# Revit family: Prises non verrouillées saillies 200_250V
name_source: partatom
category: Installations électriques
revit_build: Autodesk Revit 2018 (Build: 20170223_1515(x64)
units: mm (PartAtom-declared; Revit-internal decimal feet)

## family parameters
Conserver l'orientation des annotations = Non
Cote de connecteur circulaire = Utiliser le diamètre
Couper avec des vides une fois chargée = Non
Hôte = Face
Partagée = Non
Point de calcul de pièce = Non
Type d'élément = Normal

## types (17) — shared parameters
Couleur caractéristique = bleu
Elévation par défaut = 1000 mm  [stored 3.28084 ft]
Fabricant = Legrand
Famille produit = 0854-P17 TEMPRA PRO
Prise au standard international pour montage encastré ou saillie avec accessoire permet la connexion d'appareils de puissance = Prise au standard international pour montage encastré ou saillie avec accessoire permet la connexion d'appareils de puissance
Standard CEI ou NFC = CEI
Température maximum d'utilisation = 40
Température minimum d'installation = -5
Température minimum d'utilisation = -25
Tension V = 230 V  50/60 Hz  bleu
Type de cerrouillage = x
matériau du boitier = plastique
résistance aux chocs IK = 9
type de raccordement = bornes à vis

## per-type parameters (varying)
| type | Description | Diamètre entrée de câble | Intensité A | Modèle | Nombre de pôles | Position de la Terre h | classe de protection IP | entraxe de fixation horizontal mm | entraxe de fixation vertical mm | hauteur mm | largeur mm | profondeur mm | sans halogène |
| IDS_LG_090167 | IDS_DESCRIPTION_LG_090167 | M20/M25 | 16 A | LG-090167 | 3 | 6 | IP44 | 70 mm | 0 mm  [stored 0 ft] | 147 mm | 93 mm | 139 mm | Oui |
| IDS_LG_090180 | IDS_DESCRIPTION_LG_090180 | M25/M32 | 32 A | LG-090180 | 3 | 6 | IP44 | 90 mm | 0 mm  [stored 0 ft] | 174 mm  [stored 0.570866 ft] | 113 mm  [stored 0.370735 ft] | 156 mm  [stored 0.511811 ft] | Oui |
| IDS_LG_555154 | IDS_DESCRIPTION_LG_555154 | M20/M25 | 16 A | LG-555154 | 3 | 6 | IP44 | 70 mm | 0 mm  [stored 0 ft] | 131 mm  [stored 0.42979 ft] | 93 mm | 125 mm  [stored 0.410105 ft] | Oui |
| IDS_LG_555155 | IDS_DESCRIPTION_LG_555155 | M20/M25 | 16 A | LG-555155 | 4 | 9 | IP44 | 70 mm | 0 mm  [stored 0 ft] | 131 mm  [stored 0.42979 ft] | 93 mm | 133 mm  [stored 0.436352 ft] | Oui |
| IDS_LG_555156 | IDS_DESCRIPTION_LG_555156 | M20/M25 | 16 A | LG-555156 | 5 | 9 | IP44 | 70 mm | 0 mm  [stored 0 ft] | 131 mm  [stored 0.42979 ft] | 93 mm | 139 mm | Oui |
| IDS_LG_555254 | IDS_DESCRIPTION_LG_555254 | M25/M32 | 32 A | LG-555254 | 3 | 6 | IP44 | 90 mm | 0 mm  [stored 0 ft] | 174 mm  [stored 0.570866 ft] | 113 mm  [stored 0.370735 ft] | 156 mm  [stored 0.511811 ft] | Oui |
| IDS_LG_555255 | IDS_DESCRIPTION_LG_555255 | M25/M32 | 32 A | LG-555255 | 4 | 9 | IP44 | 90 mm | 0 mm  [stored 0 ft] | 156 mm  [stored 0.511811 ft] | 113 mm  [stored 0.370735 ft] | 155 mm | Oui |
| IDS_LG_555256 | IDS_DESCRIPTION_LG_555256 | M25/M32 | 32 A | LG-555256 | 5 | 9 | IP44 | 90 mm | 0 mm  [stored 0 ft] | 156 mm  [stored 0.511811 ft] | 113 mm  [stored 0.370735 ft] | 161 mm | Oui |
| IDS_LG_555354 | IDS_DESCRIPTION_LG_555354 | M20/M25 | 16 A | LG-555354 | 3 | 6 |  | 70 mm | 0 mm  [stored 0 ft] | 138 mm | 93 mm | 126 mm  [stored 0.413386 ft] | Non |
| IDS_LG_555355 | IDS_DESCRIPTION_LG_555355 | M20/M25 | 16 A | LG-555355 | 4 | 9 |  | 70 mm | 0 mm  [stored 0 ft] | 138 mm | 93 mm | 134 mm  [stored 0.439633 ft] | Non |
| IDS_LG_555356 | IDS_DESCRIPTION_LG_555356 | M20/M25 | 16 A | LG-555356 | 5 | 9 |  | 70 mm | 0 mm  [stored 0 ft] | 138 mm | 93 mm | 140 mm | Non |
| IDS_LG_555454 | IDS_DESCRIPTION_LG_555454 | M25/M32 | 32 A | LG-555454 | 3 | 6 |  | 90 mm | 0 mm  [stored 0 ft] | 163 mm  [stored 0.534777 ft] | 113 mm  [stored 0.370735 ft] | 156 mm  [stored 0.511811 ft] | Non |
| IDS_LG_555455 | IDS_DESCRIPTION_LG_555455 | M25/M32 | 32 A | LG-555455 | 4 | 9 |  | 90 mm | 0 mm  [stored 0 ft] | 163 mm  [stored 0.534777 ft] | 113 mm  [stored 0.370735 ft] | 156 mm  [stored 0.511811 ft] | Non |
| IDS_LG_555456 | IDS_DESCRIPTION_LG_555456 | M25/M32 | 32 A | LG-555456 | 5 | 9 |  | 90 mm | 0 mm  [stored 0 ft] | 163 mm  [stored 0.534777 ft] | 113 mm  [stored 0.370735 ft] | 162 mm | Non |
| IDS_LG_555554 | IDS_DESCRIPTION_LG_555554 | M32 | 63 A | LG-555554 | 3 | 6 |  | 119 mm  [stored 0.39042 ft] | 156 mm  [stored 0.511811 ft] | 270 mm  [stored 0.885827 ft] | 130 mm | 190 mm | Non |
| IDS_LG_555555 | IDS_DESCRIPTION_LG_555555 | M32 | 63 A | LG-555555 | 4 | 9 |  | 119 mm  [stored 0.39042 ft] | 156 mm  [stored 0.511811 ft] | 270 mm  [stored 0.885827 ft] | 130 mm | 190 mm | Non |
| IDS_LG_555556 | IDS_DESCRIPTION_LG_555556 | M32 | 63 A | LG-555556 | 5 | 9 |  | 119 mm  [stored 0.39042 ft] | 156 mm  [stored 0.511811 ft] | 270 mm  [stored 0.885827 ft] | 130 mm | 190 mm | Non |

note: [stored X ft] marks values corroborated as IEEE doubles in the binary element streams (Revit-internal decimal feet)
